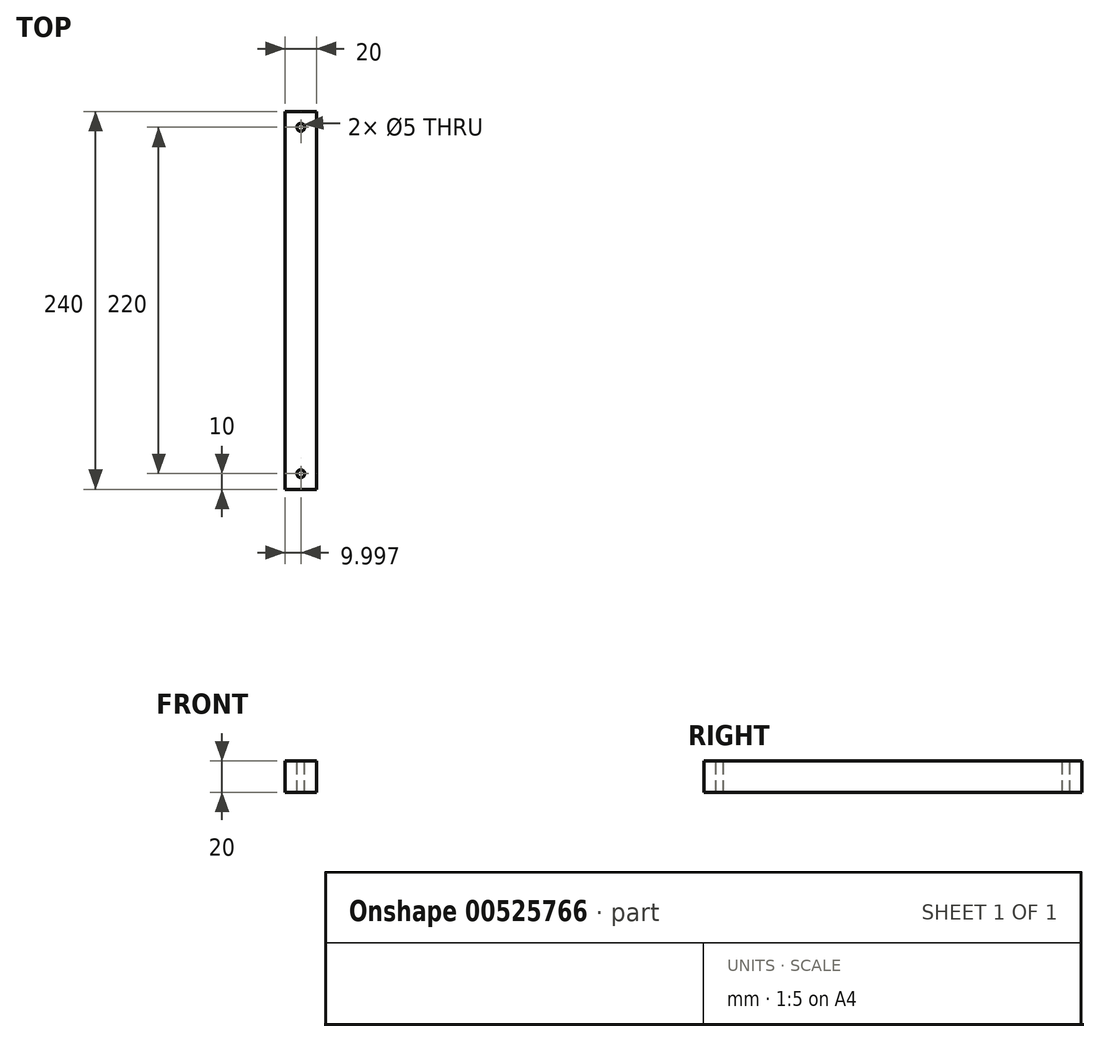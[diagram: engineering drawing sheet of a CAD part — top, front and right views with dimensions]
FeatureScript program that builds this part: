
annotation { "Feature Type Name" : "Feature", "Feature Type Description" : "" }
export const myFeature = defineFeature(function(context is Context, id is Id, definition is map)
    precondition{}
    {
        {
            var Q0;
            Q0=qCreatedBy(makeId("Front.planeOp"),FACE);
            var sketch = newSketch(context, id + "F0", { "sketchPlane" : qUnion([Q0])});
            skLineSegment(sketch, "E0.bottom", {"start": v(14.68, -12.3) * mm, "end": v(34.68, -12.3) * mm});
            skLineSegment(sketch, "E0.top", {"start": v(14.68, -32.3) * mm, "end": v(34.68, -32.3) * mm});
            skLineSegment(sketch, "E0.left", {"start": v(14.68, -12.3) * mm, "end": v(14.68, -32.3) * mm});
            skLineSegment(sketch, "E0.right", {"start": v(34.68, -12.3) * mm, "end": v(34.68, -32.3) * mm});
            skSolve(sketch);
        }
        {
            var Q0;
            Q0 = qSketchRegion(id + "F0", true);
            extrude(context, id + "F1", {"entities" : qUnion([Q0]), "depth" : 240 * mm, "offsetDistance" : 25 * mm});
        }
        {
            var Q0;
            Q0=makeQuery(id+"F1.opExtrude","SWEPT_FACE",FACE,{"disambiguationData":[OSD([sQuery(id+"F0.wireOp",EDGE,"E0.bottom")])]});
            var sketch = newSketch(context, id + "F2", { "sketchPlane" : qUnion([Q0])});
            skCircle(sketch, "E1", {"center": v(24.68, -230) * mm, "radius": 2.5 * mm});
            skSolve(sketch);
        }
        {
            var Q0;
            Q0=makeQuery(id+"F2.imprint","IMPRINT",FACE,{"disambiguationData":[TD([[makeQuery(id+"F2.imprint","IMPRINT",EDGE,{"derivedFrom":sQuery(id+"F2.wireOp",EDGE,"E1")}),1.0]])]});
            extrude(context, id + "F3", {"entities" : qUnion([Q0]), "operationType" : NewBodyOperationType.REMOVE, "oppositeDirection" : true, "depth" : 25 * mm, "offsetDistance" : 25 * mm});
        }
        {
            var Q0;
            Q0=makeQuery(id+"F1.opExtrude","SWEPT_FACE",FACE,{"disambiguationData":[OSD([sQuery(id+"F0.wireOp",EDGE,"E0.bottom")])]});
            var sketch = newSketch(context, id + "F4", { "sketchPlane" : qUnion([Q0])});
            skCircle(sketch, "E2", {"center": v(24.68, -10) * mm, "radius": 2.5 * mm});
            skSolve(sketch);
        }
        {
            var Q0;
            Q0 = qSketchRegion(id + "F4", true);
            extrude(context, id + "F5", {"entities" : qUnion([Q0]), "operationType" : NewBodyOperationType.REMOVE, "oppositeDirection" : true, "depth" : 25 * mm, "offsetDistance" : 25 * mm});
        }
    });
